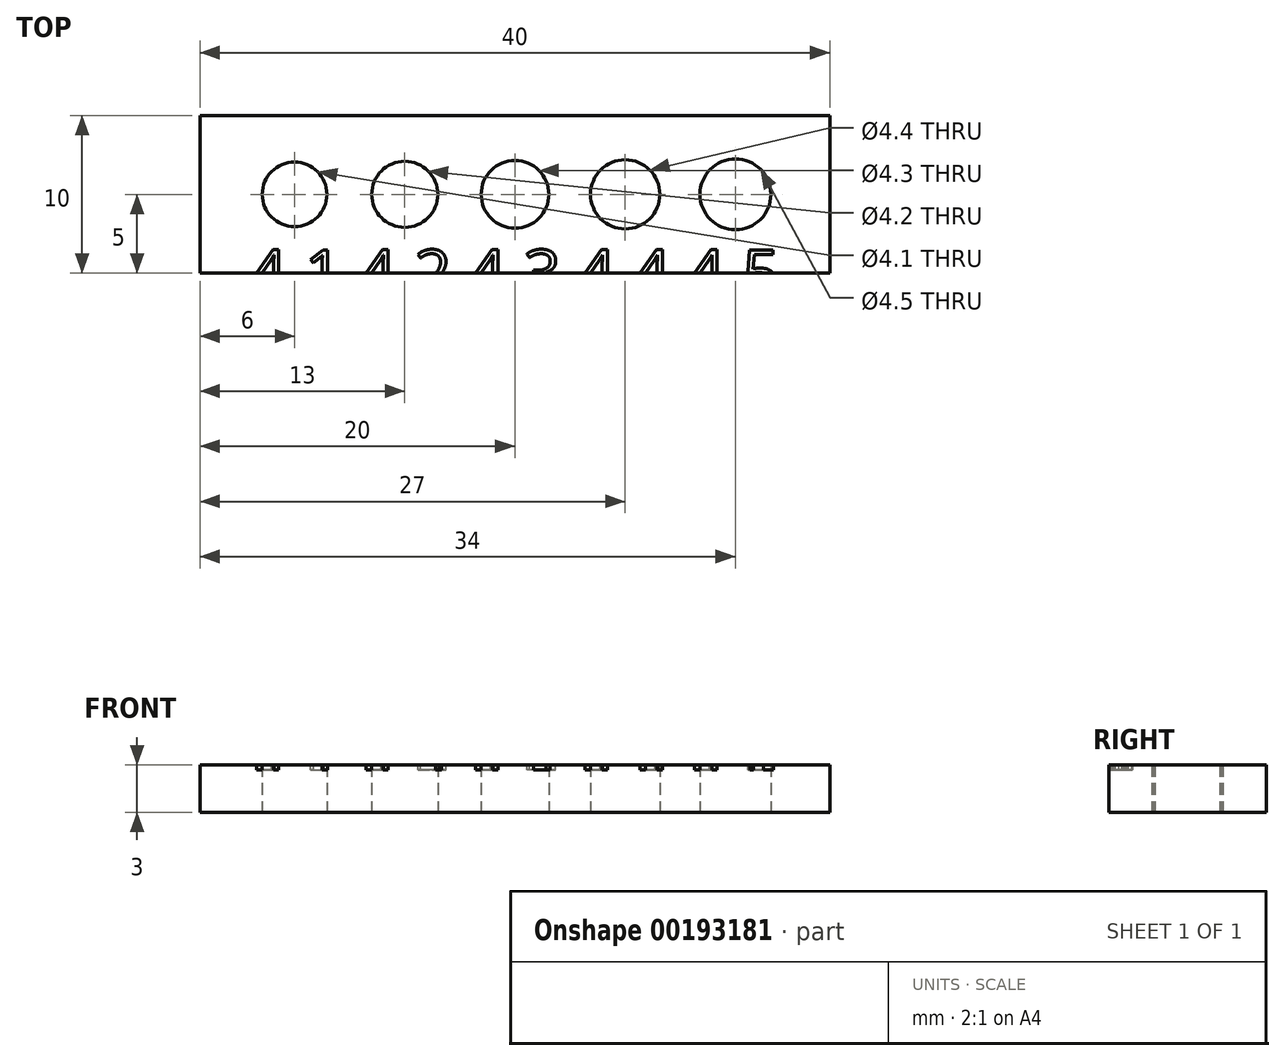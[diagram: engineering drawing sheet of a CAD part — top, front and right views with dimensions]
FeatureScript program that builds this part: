
annotation { "Feature Type Name" : "Feature", "Feature Type Description" : "" }
export const myFeature = defineFeature(function(context is Context, id is Id, definition is map)
    precondition{}
    {
        {
            var Q0;
            Q0=qCreatedBy(makeId("Top.planeOp"),FACE);
            var sketch = newSketch(context, id + "F0", { "sketchPlane" : qUnion([Q0])});
            skCircle(sketch, "E0", {"center": v(-14, 0) * mm, "radius": 2.05 * mm});
            skLineSegment(sketch, "E1.bottom", {"start": v(20, 5) * mm, "end": v(-20, 5) * mm});
            skLineSegment(sketch, "E1.top", {"start": v(20, -5) * mm, "end": v(-20, -5) * mm});
            skLineSegment(sketch, "E1.left", {"start": v(20, 5) * mm, "end": v(20, -5) * mm});
            skLineSegment(sketch, "E1.right", {"start": v(-20, 5) * mm, "end": v(-20, -5) * mm});
            skCircle(sketch, "E2", {"center": v(-7, 0) * mm, "radius": 2.1 * mm});
            skCircle(sketch, "E3", {"center": v(0, 0) * mm, "radius": 2.15 * mm});
            skCircle(sketch, "E4", {"center": v(7, 0) * mm, "radius": 2.2 * mm});
            skCircle(sketch, "E5", {"center": v(14, 0) * mm, "radius": 2.25 * mm});
            skSolve(sketch);
        }
        {
            var Q0;
            Q0 = qSketchRegion(id + "F0", true);
            extrude(context, id + "F1", {"entities" : qUnion([Q0]), "depth" : 3 * mm});
        }
        {
            var Q0;
            Q0=makeQuery(id+"F1.opExtrude","CAP_FACE",FACE,{"disambiguationData":[OSD([sQuery(id+"F0.wireOp",EDGE,"E0"),sQuery(id+"F0.wireOp",EDGE,"E1.bottom"),sQuery(id+"F0.wireOp",EDGE,"E1.top"),sQuery(id+"F0.wireOp",EDGE,"E1.left"),sQuery(id+"F0.wireOp",EDGE,"E1.right"),sQuery(id+"F0.wireOp",EDGE,"E2"),sQuery(id+"F0.wireOp",EDGE,"E3"),sQuery(id+"F0.wireOp",EDGE,"E4"),sQuery(id+"F0.wireOp",EDGE,"E5")])],"isStart":false});
            var sketch = newSketch(context, id + "F2", { "sketchPlane" : qUnion([Q0])});
            skPoint(sketch, "E6.middle", {"position": v(0, 0) * mm});
            skText(sketch, "E7", { "text": "4.1 4.2 4.3 4.4 4.5", "fontName": "OpenSans-Regular.ttf"});
            const initialGuessF2  = {"E7": [-0.01686, -0.0065, 1, 0, 0.003]};
            skSetInitialGuess(sketch, initialGuessF2);
            skSolve(sketch);
        }
        {
            var Q0;
            Q0 = qSketchRegion(id + "F2", true);
            extrude(context, id + "F3", {"entities" : qUnion([Q0]), "operationType" : NewBodyOperationType.REMOVE, "oppositeDirection" : true, "depth" : 0.3 * mm});
        }
    });
